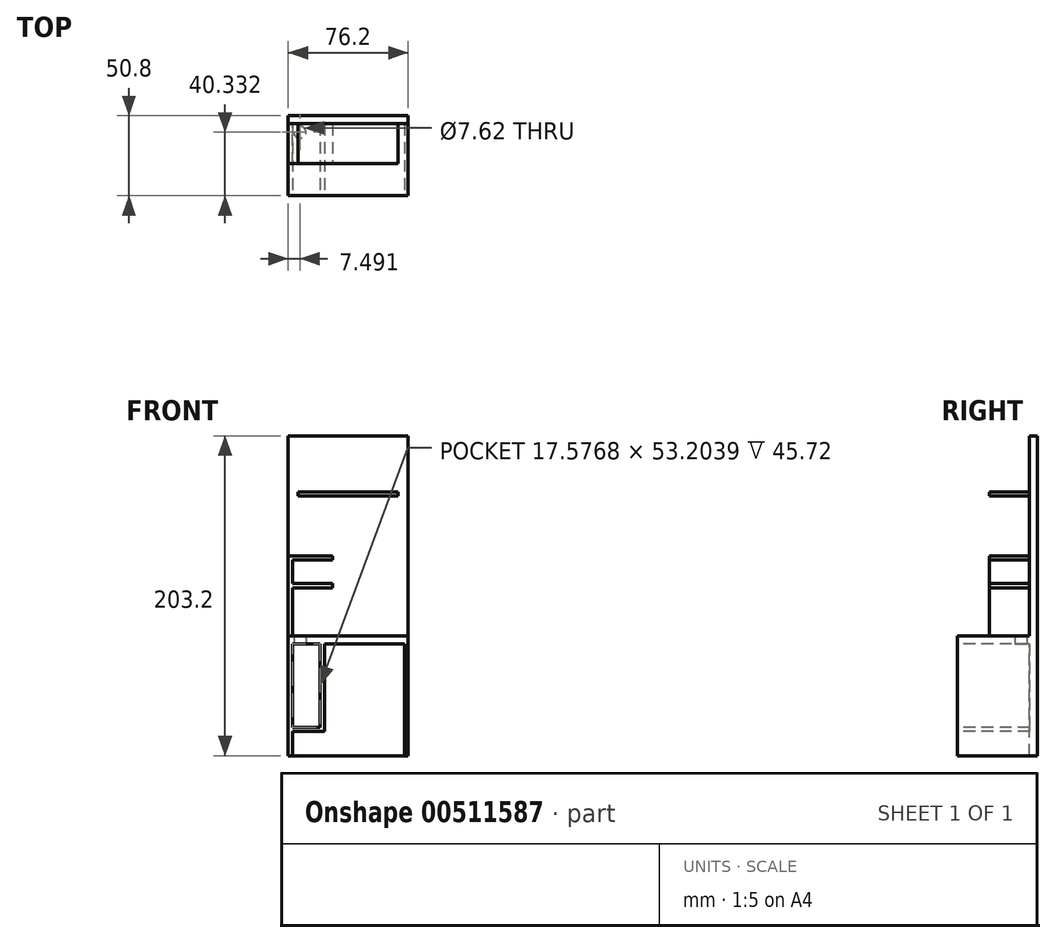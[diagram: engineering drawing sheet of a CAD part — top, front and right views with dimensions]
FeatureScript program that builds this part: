
annotation { "Feature Type Name" : "Feature", "Feature Type Description" : "" }
export const myFeature = defineFeature(function(context is Context, id is Id, definition is map)
    precondition{}
    {
        {
            var Q0;
            Q0=qCreatedBy(makeId("Top.planeOp"),FACE);
            var sketch = newSketch(context, id + "F0", { "sketchPlane" : qUnion([Q0])});
            skLineSegment(sketch, "E0.bottom", {"start": v(-38.1, -25.4) * mm, "end": v(38.1, -25.4) * mm});
            skLineSegment(sketch, "E0.top", {"start": v(-38.1, 25.4) * mm, "end": v(38.1, 25.4) * mm});
            skLineSegment(sketch, "E0.left", {"start": v(-38.1, -25.4) * mm, "end": v(-38.1, 25.4) * mm});
            skLineSegment(sketch, "E0.right", {"start": v(38.1, -25.4) * mm, "end": v(38.1, 25.4) * mm});
            skPoint(sketch, "E0.middle", {"position": v(0, 0) * mm});
            skSolve(sketch);
        }
        {
            var Q0;
            Q0=makeQuery(id+"F0.imprint","IMPRINT",FACE,{"disambiguationData":[TD([[makeQuery(id+"F0.imprint","IMPRINT",EDGE,{"derivedFrom":sQuery(id+"F0.wireOp",EDGE,"E0.bottom")}),1.0]])]});
            extrude(context, id + "F1", {"entities" : qUnion([Q0]), "depth" : 76.2 * mm});
        }
        {
            var Q0;
            Q0=makeQuery(id+"F1.opExtrude","SWEPT_FACE",FACE,{"disambiguationData":[OSD([sQuery(id+"F0.wireOp",EDGE,"E0.bottom")])]});
            var sketch = newSketch(context, id + "F2", { "sketchPlane" : qUnion([Q0])});
            skLineSegment(sketch, "E1.bottom", {"start": v(-35.36, 0) * mm, "end": v(35.76, 0) * mm});
            skLineSegment(sketch, "E1.top", {"start": v(-35.36, 71.12) * mm, "end": v(35.76, 71.12) * mm});
            skLineSegment(sketch, "E1.left", {"start": v(-35.36, 0) * mm, "end": v(-35.36, 71.12) * mm});
            skLineSegment(sketch, "E1.right", {"start": v(35.76, 0) * mm, "end": v(35.76, 71.12) * mm});
            skSolve(sketch);
        }
        {
            var Q0;
            Q0 = qSketchRegion(id + "F2", true);
            extrude(context, id + "F3", {"entities" : qUnion([Q0]), "operationType" : NewBodyOperationType.REMOVE, "oppositeDirection" : true, "depth" : 45.72 * mm});
        }
        {
            var Q0;
            Q0=makeQuery(id+"F1.opExtrude","CAP_FACE",FACE,{"disambiguationData":[OSD([sQuery(id+"F0.wireOp",EDGE,"E0.bottom"),sQuery(id+"F0.wireOp",EDGE,"E0.top"),sQuery(id+"F0.wireOp",EDGE,"E0.left"),sQuery(id+"F0.wireOp",EDGE,"E0.right")])],"isStart":false});
            var sketch = newSketch(context, id + "F4", { "sketchPlane" : qUnion([Q0])});
            skLineSegment(sketch, "E2.bottom", {"start": v(-38.1, 25.4) * mm, "end": v(38.1, 25.4) * mm});
            skLineSegment(sketch, "E2.top", {"start": v(-38.1, 20.32) * mm, "end": v(38.1, 20.32) * mm});
            skLineSegment(sketch, "E2.left", {"start": v(-38.1, 25.4) * mm, "end": v(-38.1, 20.32) * mm});
            skLineSegment(sketch, "E2.right", {"start": v(38.1, 25.4) * mm, "end": v(38.1, 20.32) * mm});
            skSolve(sketch);
        }
        {
            var Q0;
            Q0=makeQuery(id+"F4.imprint","IMPRINT",FACE,{"disambiguationData":[TD([[makeQuery(id+"F4.imprint","IMPRINT",EDGE,{"derivedFrom":sQuery(id+"F4.wireOp",EDGE,"E2.bottom")}),-1.0]])]});
            extrude(context, id + "F5", {"entities" : qUnion([Q0]), "operationType" : NewBodyOperationType.ADD, "depth" : 127 * mm});
        }
        {
            var Q0;
            Q0=makeQuery(id+"F5.opExtrude","SWEPT_FACE",FACE,{"disambiguationData":[OSD([sQuery(id+"F4.wireOp",EDGE,"E2.top")])]});
            var sketch = newSketch(context, id + "F6", { "sketchPlane" : qUnion([Q0])});
            skLineSegment(sketch, "E3.bottom", {"start": v(-31.72, 167.6) * mm, "end": v(31.78, 167.6) * mm});
            skLineSegment(sketch, "E3.top", {"start": v(-31.72, 165.05) * mm, "end": v(31.78, 165.05) * mm});
            skLineSegment(sketch, "E3.left", {"start": v(-31.72, 167.6) * mm, "end": v(-31.72, 165.05) * mm});
            skLineSegment(sketch, "E3.right", {"start": v(31.78, 167.6) * mm, "end": v(31.78, 165.05) * mm});
            skSolve(sketch);
        }
        {
            var Q0;
            Q0=makeQuery(id+"F6.imprint","IMPRINT",FACE,{"disambiguationData":[TD([[makeQuery(id+"F6.imprint","IMPRINT",EDGE,{"derivedFrom":sQuery(id+"F6.wireOp",EDGE,"E3.bottom")}),-1.0]])]});
            extrude(context, id + "F7", {"entities" : qUnion([Q0]), "operationType" : NewBodyOperationType.ADD, "depth" : 25.4 * mm});
        }
        {
            var Q0;
            Q0=makeQuery(id+"F0.imprint","IMPRINT",FACE,{"disambiguationData":[TD([[makeQuery(id+"F0.imprint","IMPRINT",EDGE,{"derivedFrom":sQuery(id+"F0.wireOp",EDGE,"E0.bottom")}),1.0]])]});
            var sketch = newSketch(context, id + "F8", { "sketchPlane" : qUnion([Q0])});
            skCircle(sketch, "E4", {"center": v(-30.6, 14.93) * mm, "radius": 3.81 * mm});
            skSolve(sketch);
        }
        {
            var Q0;
            Q0 = qSketchRegion(id + "F8", true);
            extrude(context, id + "F9", {"entities" : qUnion([Q0]), "operationType" : NewBodyOperationType.REMOVE, "depth" : 112.27 * mm});
        }
        {
            var Q0;
            Q0=makeQuery(id+"F2.imprint","IMPRINT",FACE,{"disambiguationData":[TD([[makeQuery(id+"F2.imprint","IMPRINT",EDGE,{"derivedFrom":sQuery(id+"F2.wireOp",EDGE,"E1.bottom")}),1.0]])]});
            var sketch = newSketch(context, id + "F10", { "sketchPlane" : qUnion([Q0])});
            skLineSegment(sketch, "E5.bottom", {"start": v(-35.36, 17.92) * mm, "end": v(-15.04, 17.92) * mm});
            skLineSegment(sketch, "E5.top", {"start": v(-35.36, 15.38) * mm, "end": v(-15.04, 15.38) * mm});
            skLineSegment(sketch, "E5.left", {"start": v(-35.36, 17.92) * mm, "end": v(-35.36, 15.38) * mm});
            skLineSegment(sketch, "E5.right", {"start": v(-15.04, 17.92) * mm, "end": v(-15.04, 15.38) * mm});
            skSolve(sketch);
        }
        {
            var Q0;
            Q0=makeQuery(id+"F10.imprint","IMPRINT",FACE,{"disambiguationData":[TD([[makeQuery(id+"F10.imprint","IMPRINT",EDGE,{"derivedFrom":sQuery(id+"F10.wireOp",EDGE,"E5.bottom")}),-1.0]])]});
            extrude(context, id + "F11", {"entities" : qUnion([Q0]), "operationType" : NewBodyOperationType.ADD, "oppositeDirection" : true, "depth" : 45.72 * mm});
        }
        {
            var Q0;
            {var subQ0=sQuery(id+"F4.wireOp",EDGE,"E2.top");Q0=makeQuery(id+"F4.imprint","IMPRINT",FACE,{"disambiguationData":[TD([[makeQuery(id+"F4.imprint","IMPRINT",EDGE,{"derivedFrom":subQ0}),-1.0]])]});}
            var sketch = newSketch(context, id + "F12", { "sketchPlane" : qUnion([Q0])});
            skLineSegment(sketch, "E6.bottom", {"start": v(-38.1, 20.32) * mm, "end": v(-35.36, 20.32) * mm});
            skLineSegment(sketch, "E6.top", {"start": v(-38.1, -5.08) * mm, "end": v(-35.36, -5.08) * mm});
            skLineSegment(sketch, "E6.left", {"start": v(-38.1, 20.32) * mm, "end": v(-38.1, -5.08) * mm});
            skLineSegment(sketch, "E6.right", {"start": v(-35.36, 20.32) * mm, "end": v(-35.36, -5.08) * mm});
            skSolve(sketch);
        }
        {
            var Q0;
            Q0 = qSketchRegion(id + "F12", true);
            extrude(context, id + "F13", {"entities" : qUnion([Q0]), "operationType" : NewBodyOperationType.ADD, "depth" : 50.8 * mm});
        }
        {
            var Q0;
            Q0=makeQuery(id+"F13.opExtrude","SWEPT_FACE",FACE,{"disambiguationData":[OSD([sQuery(id+"F12.wireOp",EDGE,"E6.right")])]});
            var sketch = newSketch(context, id + "F14", { "sketchPlane" : qUnion([Q0])});
            skLineSegment(sketch, "E7.bottom", {"start": v(-5.08, 127) * mm, "end": v(20.32, 127) * mm});
            skLineSegment(sketch, "E7.top", {"start": v(-5.08, 124.26) * mm, "end": v(20.32, 124.26) * mm});
            skLineSegment(sketch, "E7.left", {"start": v(-5.08, 127) * mm, "end": v(-5.08, 124.26) * mm});
            skLineSegment(sketch, "E7.right", {"start": v(20.32, 127) * mm, "end": v(20.32, 124.26) * mm});
            skSolve(sketch);
        }
        {
            var Q0;
            Q0=makeQuery(id+"F14.imprint","IMPRINT",FACE,{"disambiguationData":[TD([[makeQuery(id+"F14.imprint","IMPRINT",EDGE,{"derivedFrom":sQuery(id+"F14.wireOp",EDGE,"E7.bottom")}),1.0]])]});
            extrude(context, id + "F15", {"entities" : qUnion([Q0]), "operationType" : NewBodyOperationType.ADD, "depth" : 25.4 * mm});
        }
        {
            var Q0;
            Q0=makeQuery(id+"F13.opExtrude","SWEPT_FACE",FACE,{"disambiguationData":[OSD([sQuery(id+"F12.wireOp",EDGE,"E6.right")])]});
            var sketch = newSketch(context, id + "F16", { "sketchPlane" : qUnion([Q0])});
            skLineSegment(sketch, "E8.bottom", {"start": v(-5.08, 109.31) * mm, "end": v(20.32, 109.31) * mm});
            skLineSegment(sketch, "E8.top", {"start": v(-5.08, 106.57) * mm, "end": v(20.32, 106.57) * mm});
            skLineSegment(sketch, "E8.left", {"start": v(-5.08, 109.31) * mm, "end": v(-5.08, 106.57) * mm});
            skLineSegment(sketch, "E8.right", {"start": v(20.32, 109.31) * mm, "end": v(20.32, 106.57) * mm});
            skSolve(sketch);
        }
        {
            var Q0;
            Q0=makeQuery(id+"F16.imprint","IMPRINT",FACE,{"disambiguationData":[TD([[makeQuery(id+"F16.imprint","IMPRINT",EDGE,{"derivedFrom":sQuery(id+"F16.wireOp",EDGE,"E8.bottom")}),-1.0]])]});
            extrude(context, id + "F17", {"entities" : qUnion([Q0]), "operationType" : NewBodyOperationType.ADD, "depth" : 25.4 * mm});
        }
        {
            var Q0;
            Q0=makeQuery(id+"F0.imprint","IMPRINT",FACE,{"disambiguationData":[TD([[makeQuery(id+"F0.imprint","IMPRINT",EDGE,{"derivedFrom":sQuery(id+"F0.wireOp",EDGE,"E0.bottom")}),1.0]])]});
            var sketch = newSketch(context, id + "F18", { "sketchPlane" : qUnion([Q0])});
            skLineSegment(sketch, "E9.bottom", {"start": v(-15.04, 20.32) * mm, "end": v(-17.78, 20.32) * mm});
            skLineSegment(sketch, "E9.top", {"start": v(-15.04, -25.4) * mm, "end": v(-17.78, -25.4) * mm});
            skLineSegment(sketch, "E9.left", {"start": v(-15.04, 20.32) * mm, "end": v(-15.04, -25.4) * mm});
            skLineSegment(sketch, "E9.right", {"start": v(-17.78, 20.32) * mm, "end": v(-17.78, -25.4) * mm});
            skSolve(sketch);
        }
        {
            var Q0;
            Q0 = qSketchRegion(id + "F18", true);
            extrude(context, id + "F19", {"entities" : qUnion([Q0]), "operationType" : NewBodyOperationType.ADD, "depth" : 71.12 * mm});
        }
        {
            var Q0;
            Q0=makeQuery(id+"F2.imprint","IMPRINT",FACE,{"disambiguationData":[TD([[makeQuery(id+"F2.imprint","IMPRINT",EDGE,{"derivedFrom":sQuery(id+"F2.wireOp",EDGE,"E1.bottom")}),1.0]])]});
            var sketch = newSketch(context, id + "F20", { "sketchPlane" : qUnion([Q0])});
            skLineSegment(sketch, "E10.bottom", {"start": v(-17.78, 0) * mm, "end": v(-15.04, 0) * mm});
            skLineSegment(sketch, "E10.top", {"start": v(-17.78, 0) * mm, "end": v(-15.04, 0) * mm});
            skLineSegment(sketch, "E10.left", {"start": v(-17.78, 0) * mm, "end": v(-17.78, 0) * mm});
            skLineSegment(sketch, "E10.right", {"start": v(-15.04, 0) * mm, "end": v(-15.04, 0) * mm});
            skLineSegment(sketch, "E11.bottom", {"start": v(-17.78, 15.38) * mm, "end": v(-15.04, 15.38) * mm});
            skLineSegment(sketch, "E11.left", {"start": v(-17.78, 15.38) * mm, "end": v(-17.78, 0) * mm});
            skLineSegment(sketch, "E11.right", {"start": v(-15.04, 15.38) * mm, "end": v(-15.04, 0) * mm});
            skSolve(sketch);
        }
        {
            var Q0;
            Q0 = qSketchRegion(id + "F20", true);
            extrude(context, id + "F21", {"entities" : qUnion([Q0]), "operationType" : NewBodyOperationType.REMOVE, "oppositeDirection" : true, "depth" : 45.72 * mm});
        }
    });
